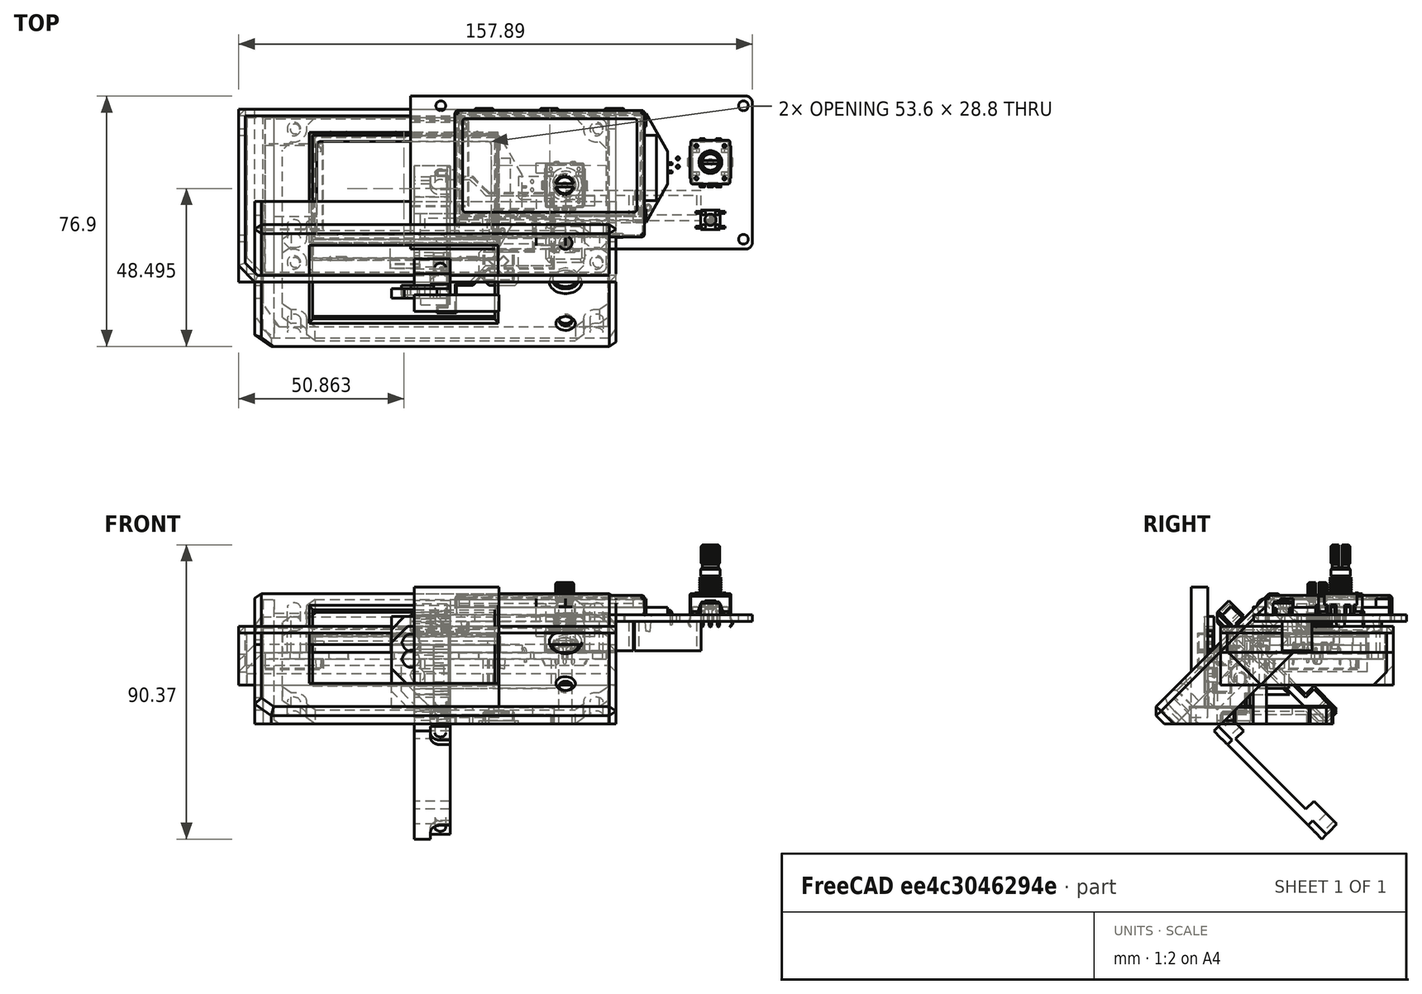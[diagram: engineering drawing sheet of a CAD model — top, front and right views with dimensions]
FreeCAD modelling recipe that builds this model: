
FCSTD DOCUMENT  (FreeCAD 0.18R16146 (Git))
Label: lcd-mount
License: All rights reserved
LicenseURL: http://en.wikipedia.org/wiki/All_rights_reserved
objects: Part::Box×50, Part::Chamfer×35, Part::Feature×26, Part::Cylinder×20, Part::Cut×20, Part::MultiFuse×19, App::Part×2, Part::Fillet×2
note: 172 computed .brp shape members not serialized (recipe doc carries the construction recipe); baked Part::Feature solids carry a one-line shape summary decoded from their .brp

FEATURE [Part::Feature] Part__Feature  label="backlight"
  Placement = pos=(66.893,35.0548,33.5073) rot=(0,0.707107,0.707107;3.14159rad)
  shape: bbox 66.3 x 33.5 x 10 mm, 77 faces (baked)
FEATURE [Part::Feature] Part__Feature001  label="lcd"
  Placement = pos=(30.968,36.0048,35.8073) rot=(1,0,0;1.5708rad)
  shape: bbox 56.5 x 40.6 x 5.3 mm, 42 faces (baked)
FEATURE [Part::Feature] Part__Feature002  label="PCB"
  Placement = pos=(40.393,33.6048,31.5073) rot=(0,0,1;0rad)
  shape: bbox 105 x 47 x 11 mm, 65 faces (baked)
FEATURE [Part::Feature] Part__Feature003  label="Tactal Switch - SMD (6mmx 6mmx 4"
  Placement = pos=(80.0049,19.0968,33.5073) rot=(0,0,1;0rad)
  shape: bbox 9.017 x 6.169 x 4.3 mm, 213 faces (baked)
FEATURE [Part::Feature] Part__Feature004  label="pec11r-4215k_l13-8_w12-4_h21-5"
  Placement = pos=(80.0049,36.8224,33.5073) rot=(1,0,0;1.5708rad)
  shape: bbox 13.86 x 14.85 x 25.2 mm, 388 faces (baked)
FEATURE [Part::Feature] Part__Feature005  label="LCD bezel"
  Placement = pos=(40.1054,33.7331,33.5073) rot=(0,0,1;0rad)
  shape: bbox 58.3 x 38.9 x 6 mm, 31 faces (baked)
FEATURE [App::Part] _2864Amini  label="12864Amini"
  Group = -> [Part__Feature,Part__Feature001,Part__Feature002,Part__Feature003,Part__Feature004,Part__Feature005]
  Origin = -> Origin
  Placement = pos=(128.127,156.765,-6.05529) rot=(0,0,1;0rad)
FEATURE [App::Part] Fysetc_12864_Display_Fysetc_Mini_12864_v1_v2  label="Fysetc_12864_Display_Fysetc Mini 12864 v1 v2"
  Group = -> [_2864Amini]
  Origin = -> Origin001
FEATURE [Part::Feature] Part__Feature005001  label="LCD bezel001"
  Placement = pos=(40.1054,33.7331,33.5073) rot=(0,0,1;0rad)
  shape: bbox 58.3 x 38.9 x 6 mm, 31 faces (baked)
FEATURE [Part::Feature] Part__Feature004001  label="pec11r-4215k_l13-8_w12-4_h21-006"
  Placement = pos=(80.0049,36.8224,33.5073) rot=(1,0,0;1.5708rad)
  shape: bbox 13.86 x 14.85 x 25.2 mm, 388 faces (baked)
FEATURE [Part::Feature] Part__Feature003001  label="Tactal Switch - SMD (6mmx 6mmx 005"
  Placement = pos=(80.0049,19.0968,33.5073) rot=(0,0,1;0rad)
  shape: bbox 9.017 x 6.169 x 4.3 mm, 213 faces (baked)
FEATURE [Part::Feature] Part__Feature002001  label="PCB001"
  Placement = pos=(40.393,33.6048,31.5073) rot=(0,0,1;0rad)
  shape: bbox 105 x 47 x 11 mm, 65 faces (baked)
FEATURE [Part::Feature] Part__Feature001001  label="lcd001"
  Placement = pos=(30.968,36.0048,35.8073) rot=(1,0,0;1.5708rad)
  shape: bbox 56.5 x 40.6 x 5.3 mm, 42 faces (baked)
FEATURE [Part::Feature] Part__Feature005002  label="backlight001"
  Placement = pos=(66.893,35.0548,33.5073) rot=(0,0.707107,0.707107;3.14159rad)
  shape: bbox 66.3 x 33.5 x 10 mm, 77 faces (baked)
FEATURE [Part::MultiFuse] Fusion
  Placement = pos=(-44.78,-7.11,-11.51) rot=(0,0,1;0rad)
  Shapes = -> [Part__Feature005002,Part__Feature001001,Part__Feature002001,Part__Feature003001,Part__Feature004001,Part__Feature005001]
FEATURE [Part::Box] Box  label="Cube"
  AttacherType = Attacher::AttachEngine3D
  Height = 2
  Length = 116
  Placement = pos=(-65,0,28) rot=(0,0,1;0rad)
  Width = 53
FEATURE [Part::Box] Box001  label="Cube001"
  AttacherType = Attacher::AttachEngine3D
  Height = 4
  Length = 56
  Placement = pos=(-42.25,13,28) rot=(0,0,1;0rad)
  Width = 32
FEATURE [Part::Cylinder] Cylinder
  Angle = 360
  AttacherType = Attacher::AttachEngine3D
  Height = 6
  Placement = pos=(45,6,20) rot=(0,0,1;0rad)
  Radius = 2.05
FEATURE [Part::Cylinder] Cylinder001
  Angle = 360
  AttacherType = Attacher::AttachEngine3D
  Height = 6
  Placement = pos=(45,47,20) rot=(0,0,1;0rad)
  Radius = 2.05
FEATURE [Part::Cylinder] Cylinder002
  Angle = 360
  AttacherType = Attacher::AttachEngine3D
  Height = 6
  Placement = pos=(-48,47,20) rot=(0,0,1;0rad)
  Radius = 2.05
FEATURE [Part::Cylinder] Cylinder003
  Angle = 360
  AttacherType = Attacher::AttachEngine3D
  Height = 6
  Placement = pos=(-48,6,20) rot=(0,0,1;0rad)
  Radius = 2.05
FEATURE [Part::Cylinder] Cylinder004
  Angle = 360
  AttacherType = Attacher::AttachEngine3D
  Height = 6
  Placement = pos=(-48,47,22) rot=(0,0,1;0rad)
  Radius = 4
FEATURE [Part::Cylinder] Cylinder005
  Angle = 360
  AttacherType = Attacher::AttachEngine3D
  Height = 6
  Placement = pos=(-48,6,22) rot=(0,0,1;0rad)
  Radius = 4
FEATURE [Part::Cylinder] Cylinder006
  Angle = 360
  AttacherType = Attacher::AttachEngine3D
  Height = 6
  Placement = pos=(45,47,22) rot=(0,0,1;0rad)
  Radius = 4
FEATURE [Part::Cylinder] Cylinder007
  Angle = 360
  AttacherType = Attacher::AttachEngine3D
  Height = 6
  Placement = pos=(45,6,22) rot=(0,0,1;0rad)
  Radius = 4
FEATURE [Part::MultiFuse] Fusion002
  Placement = pos=(0,0,2) rot=(0,0,1;0rad)
  Shapes = -> [Cylinder003,Cylinder002,Cylinder001,Cylinder]
FEATURE [Part::Box] Box002  label="Cube002"
  AttacherType = Attacher::AttachEngine3D
  Height = 16
  Length = 2.5
  Placement = pos=(48.5,0,12) rot=(0,0,1;0rad)
  Width = 53
FEATURE [Part::Box] Box003  label="Cube003"
  AttacherType = Attacher::AttachEngine3D
  Height = 16
  Length = 2.5
  Placement = pos=(-65,0,12) rot=(0,0,1;0rad)
  Width = 53
FEATURE [Part::Box] Box004  label="Cube004"
  AttacherType = Attacher::AttachEngine3D
  Height = 16
  Length = 116
  Placement = pos=(-65,0,12) rot=(0,0,1;0rad)
  Width = 2.5
FEATURE [Part::Box] Box005  label="Cube005"
  AttacherType = Attacher::AttachEngine3D
  Height = 16
  Length = 116
  Placement = pos=(-65,50.5,12) rot=(0,0,1;0rad)
  Width = 2.5
FEATURE [Part::Box] Box006  label="Cube006"
  AttacherType = Attacher::AttachEngine3D
  Height = 6
  Length = 111
  Placement = pos=(-60,50.5,0) rot=(0,0,1;0rad)
  Width = 2.5
FEATURE [Part::Box] Box007  label="Cube007"
  AttacherType = Attacher::AttachEngine3D
  Height = 6
  Length = 111
  Placement = pos=(-60,0,0) rot=(0,0,1;0rad)
  Width = 2.5
FEATURE [Part::Box] Box008  label="Cube008"
  AttacherType = Attacher::AttachEngine3D
  Height = 6
  Length = 2.5
  Placement = pos=(-60,0,0) rot=(0,0,1;0rad)
  Width = 53
FEATURE [Part::Box] Box009  label="Cube009"
  AttacherType = Attacher::AttachEngine3D
  Height = 6
  Length = 2.5
  Placement = pos=(48.5,0,0) rot=(0,0,1;0rad)
  Width = 53
FEATURE [Part::MultiFuse] Fusion003
  Placement = pos=(0,0,22) rot=(0,0,1;0rad)
  Shapes = -> [Box009,Box008,Box007,Box006]
FEATURE [Part::Box] Box010  label="Cube010"
  AttacherType = Attacher::AttachEngine3D
  Height = 6
  Length = 2.5
  Placement = pos=(-54,0,22) rot=(0,0,1;0rad)
  Width = 53
FEATURE [Part::Feature] Fusion003001  label="Fusion004"
  shape: bbox 111 x 53 x 6 mm, 10 faces (baked)
FEATURE [Part::Chamfer] Chamfer
  Base = -> Fusion003001
  Edges = 1 edges r=5: [Edge4]
FEATURE [Part::Chamfer] Chamfer001
  Base = -> Chamfer
  Edges = 1 edges r=5: [Edge26]
FEATURE [Part::Cylinder] Cylinder008
  Angle = 360
  AttacherType = Attacher::AttachEngine3D
  Height = 37
  Placement = pos=(35.5,30,0) rot=(0,0,1;0rad)
  Radius = 4
FEATURE [Part::Cylinder] Cylinder009  label="reset-btn-pos"
  Angle = 360
  AttacherType = Attacher::AttachEngine3D
  Height = 36
  Placement = pos=(35.5,12,0) rot=(0,0,1;0rad)
  Radius = 2
FEATURE [Part::Box] Box011  label="Cube011"
  AttacherType = Attacher::AttachEngine3D
  Height = 5.5
  Length = 10
  Placement = pos=(-68,14.5,16) rot=(0,0,1;0rad)
  Width = 30.5
FEATURE [Part::MultiFuse] Fusion003005
  Shapes = -> [Cylinder004,Cylinder007,Cylinder006,Cylinder005]
FEATURE [Part::Box] Box014  label="led-pos-1"
  AttacherType = Attacher::AttachEngine3D
  Height = 10
  Length = 3
  Placement = pos=(41.5,23.5,27) rot=(0,0,1;0rad)
  Width = 3
FEATURE [Part::Box] Box015  label="led-pos-2"
  AttacherType = Attacher::AttachEngine3D
  Height = 10
  Length = 3
  Placement = pos=(26.5,33.5,27) rot=(0,0,1;0rad)
  Width = 3
FEATURE [Part::Box] Box016  label="Cube013"
  AttacherType = Attacher::AttachEngine3D
  Height = 3
  Length = 11
  Width = 47
FEATURE [Part::Box] Box017  label="Cube014"
  AttacherType = Attacher::AttachEngine3D
  Height = 3.5
  Length = 11
  Placement = pos=(0,0,-3.5) rot=(0,0,1;0rad)
  Width = 6.5
FEATURE [Part::Box] Box018  label="Cube015"
  AttacherType = Attacher::AttachEngine3D
  Height = 3.5
  Length = 11
  Placement = pos=(0,37,-3.5) rot=(0,0,1;0rad)
  Width = 10
FEATURE [Part::Cylinder] Cylinder010
  Angle = 360
  AttacherType = Attacher::AttachEngine3D
  Height = 10
  Placement = pos=(3,3,0) rot=(0,0,1;0rad)
  Radius = 1.65
FEATURE [Part::Cylinder] Cylinder011
  Angle = 360
  AttacherType = Attacher::AttachEngine3D
  Height = 10
  Placement = pos=(3,44,0) rot=(0,0,1;0rad)
  Radius = 1.65
FEATURE [Part::MultiFuse] Fusion003007003
  Placement = pos=(0,0,-6) rot=(0,0,1;0rad)
  Shapes = -> [Cylinder011,Cylinder010]
FEATURE [Part::Box] Box020  label="a2"
  AttacherType = Attacher::AttachEngine3D
  Height = 54
  Length = 128
  Placement = pos=(-70,11.8171,-5.79763) rot=(1,0,0;0.785398rad)
  Width = 13
FEATURE [Part::Feature] Box021001  label="a1"
  Placement = pos=(0,26,-1) rot=(0,0,1;0rad)
  shape: bbox 130 x 38.18 x 38.18 mm, 6 faces (baked)
FEATURE [Part::MultiFuse] Fusion003007004
  Shapes = -> [Box016,Box018,Box017]
FEATURE [Part::Cut] Cut004005004004  label="lcd-arm"
  Base = -> Fusion003007004
  Placement = pos=(0,0,0) rot=(1,0,0;3.14159rad)
  Tool = -> Fusion003007003
FEATURE [Part::Feature] Cut004005004003001  label="lcd-base001"
  Placement = pos=(0,0,-17.26) rot=(0,0,1;0rad)
  shape: bbox 111 x 44.52 x 40.02 mm, 69 faces (baked)
FEATURE [Part::Box] Box021002  label="Cube020"
  AttacherType = Attacher::AttachEngine3D
  Height = 2
  Length = 6
  Placement = pos=(0,-6,-3) rot=(0,0,1;0rad)
  Width = 6
FEATURE [Part::Box] Box021003  label="Cube021"
  AttacherType = Attacher::AttachEngine3D
  Height = 2
  Length = 6
  Placement = pos=(0,-47,-3) rot=(0,0,1;0rad)
  Width = 6
FEATURE [Part::Fillet] Fillet
  Base = -> Box021003
  Edges = 1 edges r=3: [Edge7]
FEATURE [Part::Fillet] Fillet001
  Base = -> Box021002
  Edges = 1 edges r=3: [Edge5]
FEATURE [Part::MultiFuse] Fusion003007005
  Shapes = -> [Fillet001,Fillet]
FEATURE [Part::Cut] Cut004005004003002
  Base = -> Cut004005004004
  Placement = pos=(0,0,0) rot=(0,0.382683,0.92388;3.14159rad)
  Tool = -> Fusion003007005
FEATURE [Part::Feature] Cut004005004003002001  label="Cut004005004003003"
  Placement = pos=(0,0,35.36) rot=(0,0,1;0rad)
  shape: bbox 11 x 37.83 x 37.83 mm, 20 faces (baked)
FEATURE [Part::Box] Box021005  label="Cube023"
  AttacherType = Attacher::AttachEngine3D
  Height = 10
  Length = 10
  Placement = pos=(30.5,7,23) rot=(0,0,1;0rad)
  Width = 10
FEATURE [Part::Chamfer] Chamfer012
  Base = -> Box021005
  Edges = 4 edges r=0.5: [Edge1,Edge3,Edge5,Edge7]
FEATURE [Part::Chamfer] Chamfer016  label="mounter-angle"
  Base = -> Cut004005004003002001
  Edges = 2 edges r=1.5: [Edge25,Edge27]
FEATURE [Part::Box] Box021010  label="Cube028"
  AttacherType = Attacher::AttachEngine3D
  Height = 5
  Length = 11
  Placement = pos=(-11,8,5) rot=(0,0,1;0rad)
  Width = 19
FEATURE [Part::Feature] Chamfer016001  label="mounter-angle001"
  shape: bbox 11 x 36.77 x 36.77 mm, 22 faces (baked)
FEATURE [Part::Chamfer] Chamfer016002
  Base = -> Box021010
  Edges = 1 edges r=3: [Edge12]
FEATURE [Part::Box] Box021012  label="Cube030"
  AttacherType = Attacher::AttachEngine3D
  Height = 4
  Length = 11
  Placement = pos=(-11,3,25) rot=(0,0,1;0rad)
  Width = 5
FEATURE [Part::Chamfer] Chamfer016003
  Base = -> Box021012
  Edges = 1 edges r=3: [Edge12]
FEATURE [Part::Cylinder] Cylinder013
  Angle = 360
  AttacherType = Attacher::AttachEngine3D
  Height = 10
  Placement = pos=(-3,6,15) rot=(0,-1,0;1.5708rad)
  Radius = 2
FEATURE [Part::Box] Box021011  label="Cube029"
  AttacherType = Attacher::AttachEngine3D
  Height = 22
  Length = 6
  Placement = pos=(-11,3,5) rot=(0,0,1;0rad)
  Width = 6
FEATURE [Part::Chamfer] Chamfer016004
  Base = -> Box021011
  Edges = 1 edges r=1: [Edge12]
FEATURE [Part::Cut] Cut004005004003002006
  Base = -> Chamfer016004
  Tool = -> Cylinder013
FEATURE [Part::Chamfer] Chamfer016005
  Base = -> Cut004005004003002006
  Edges = 1 edges r=1: [Edge12]
FEATURE [Part::Chamfer] Chamfer016006
  Base = -> Chamfer016002
  Edges = 1 edges r=1: [Edge12]
FEATURE [Part::MultiFuse] Fusion003007008002
  Placement = pos=(0,0,-1) rot=(0,0,1;0rad)
  Shapes = -> [Chamfer016006,Chamfer016005,Chamfer016003,Chamfer016001]
FEATURE [Part::Box] Box021013  label="Cube031"
  AttacherType = Attacher::AttachEngine3D
  Height = 19.8
  Length = 5
  Placement = pos=(-5,3,5) rot=(0,0,1;0rad)
  Width = 6
FEATURE [Part::Box] Box021014  label="Cube032"
  AttacherType = Attacher::AttachEngine3D
  Height = 5.2
  Length = 5
  Placement = pos=(-5,7.8,5) rot=(0,0,1;0rad)
  Width = 2
FEATURE [Part::Cylinder] Cylinder014
  Angle = 360
  AttacherType = Attacher::AttachEngine3D
  Height = 2
  Placement = pos=(-3e-15,6,15) rot=(0,-1,0;1.5708rad)
  Radius = 3
FEATURE [Part::Cylinder] Cylinder015
  Angle = 360
  AttacherType = Attacher::AttachEngine3D
  Height = 10
  Placement = pos=(-3e-15,6,15) rot=(0,-1,0;1.5708rad)
  Radius = 1.65
FEATURE [Part::Box] Box021015  label="Cube033"
  AttacherType = Attacher::AttachEngine3D
  Height = 40
  Length = 26
  Placement = pos=(-11,-9,2) rot=(0,0,1;0rad)
  Width = 5
FEATURE [Part::Box] Box021016  label="Cube034"
  AttacherType = Attacher::AttachEngine3D
  Height = 4
  Length = 5
  Placement = pos=(-5,-5,13) rot=(0,0,1;0rad)
  Width = 1
FEATURE [Part::Box] Box021018  label="Cube036"
  AttacherType = Attacher::AttachEngine3D
  Height = 5
  Length = 5
  Placement = pos=(-5,-4,5) rot=(0,0,1;0rad)
  Width = 7
FEATURE [Part::Box] Box021019  label="Cube037"
  AttacherType = Attacher::AttachEngine3D
  Height = 5
  Length = 5
  Placement = pos=(-5,-4,18) rot=(0,0,1;0rad)
  Width = 7
FEATURE [Part::Box] Box021020  label="Cube038"
  AttacherType = Attacher::AttachEngine3D
  Height = 18
  Length = 15
  Placement = pos=(-15,-4,5) rot=(0,0,1;0rad)
  Width = 3
FEATURE [Part::Cylinder] Cylinder016
  Angle = 360
  AttacherType = Attacher::AttachEngine3D
  Height = 10
  Placement = pos=(-10,3e-15,12) rot=(1,0,0;1.5708rad)
  Radius = 2.15
FEATURE [Part::Chamfer] Chamfer016007
  Base = -> Box021013
  Edges = 1 edges r=3: [Edge12]
FEATURE [Part::Chamfer] Chamfer016008
  Base = -> Chamfer016007
  Edges = 1 edges r=1: [Edge11]
FEATURE [Part::Cut] Cut004005004003002007
  Base = -> Chamfer016008
  Tool = -> Box021014
FEATURE [Part::Cut] Cut004005004003002008  label="back-mount"
  Base = -> Cut004005004003002007
  Placement = pos=(0,0,-1) rot=(0,0,1;0rad)
  Tool = -> Cylinder015
FEATURE [Part::Feature] Cut004005004003002008001  label="block-mount-std"
  shape: bbox 5 x 6 x 19.8 mm, 11 faces (baked)
FEATURE [Part::Cylinder] Cylinder017
  Angle = 360
  AttacherType = Attacher::AttachEngine3D
  Height = 10
  Placement = pos=(-11.8,3e-15,12) rot=(1,0,0;1.5708rad)
  Radius = 0.5
FEATURE [Part::MultiFuse] Fusion003007008003
  Placement = pos=(0,0,3) rot=(0,0,1;0rad)
  Shapes = -> [Cylinder017,Cylinder016]
FEATURE [Part::Chamfer] Chamfer016011  label="mount-arm-r1"
  Base = -> Fusion003007008002
  Edges = 2 edges r=1: [Edge99,Edge115]
FEATURE [Part::Cut] Cut004005004003002008002
  Base = -> Box021020
  Tool = -> Fusion003007008003
FEATURE [Part::Chamfer] Chamfer016012
  Base = -> Cut004005004003002008002
  Edges = 1 edges r=3: [Edge2]
FEATURE [Part::Chamfer] Chamfer016013
  Base = -> Chamfer016012
  Edges = 1 edges r=5: [Edge3]
FEATURE [Part::Feature] Fusion003007008004001  label="4040-mount001"
  shape: bbox 15 x 14 x 19.8 mm, 27 faces (baked)
FEATURE [Part::Chamfer] Chamfer016014  label="4040-mount-exp"
  Base = -> Fusion003007008004001
  Edges = 19 edges r=0.4: [Edge3,Edge9,Edge11,Edge12,Edge13,Edge32,Edge43,Edge46,Edge47,Edge51,Edge52,Edge58,Edge61,Edge62,Edge66,Edge70,Edge73,Edge74,Edge76]
FEATURE [Part::Box] Box021021  label="Cube039"
  AttacherType = Attacher::AttachEngine3D
  Height = 4
  Length = 9.5
  Placement = pos=(10.25,0.25,0) rot=(0,0,1;0rad)
  Width = 9.5
FEATURE [Part::Box] Box021022  label="Cube040"
  AttacherType = Attacher::AttachEngine3D
  Height = 1
  Length = 12
  Placement = pos=(9,-1,0) rot=(0,0,1;0rad)
  Width = 11
FEATURE [Part::Feature] Fusion003007008004003002001  label="Fusion003007008004003003"
  Placement = pos=(15,5,3) rot=(0,0,1;0rad)
  shape: bbox 5.657 x 5.657 x 10 mm, 14 faces (baked)
FEATURE [Part::Cut] Cut004005004003002008006
  Base = -> Box021021
  Tool = -> Fusion003007008004003002001
FEATURE [Part::Cylinder] Cylinder018
  Angle = 360
  AttacherType = Attacher::AttachEngine3D
  Height = 0.5
  Placement = pos=(15,5,0) rot=(0,0,1;0rad)
  Radius = 3
FEATURE [Part::Chamfer] Chamfer016020
  Base = -> Cut004005004003002008006
  Edges = 8 edges r=0.5: [Edge1,Edge2,Edge3,Edge6,Edge7,Edge8,Edge9,Edge23]
FEATURE [Part::Chamfer] Chamfer016021
  Base = -> Chamfer016020
  Edges = 12 edges r=0.2: [Edge33,Edge34,Edge35,Edge36,Edge37,Edge38,Edge39,Edge40,Edge41,Edge42,Edge43,Edge44]
FEATURE [Part::MultiFuse] Fusion003007008004003002003  label="4040-base"
  Shapes = -> [Box021016,Box021019,Box021018,Cut004005004003002008,Chamfer016013]
FEATURE [Part::Box] Box021023  label="Cube041"
  AttacherType = Attacher::AttachEngine3D
  Height = 28
  Length = 18
  Placement = pos=(-18,-5,5) rot=(0,0,1;0rad)
  Width = 3
FEATURE [Part::Box] Box021024  label="Cube042"
  AttacherType = Attacher::AttachEngine3D
  Height = 6
  Length = 9
  Placement = pos=(-9,-7,22) rot=(0,0,1;0rad)
  Width = 2
FEATURE [Part::Cylinder] Cylinder019
  Angle = 360
  AttacherType = Attacher::AttachEngine3D
  Height = 10
  Placement = pos=(-12,-10,20) rot=(-1,0,0;1.5708rad)
  Radius = 2.6
FEATURE [Part::Box] Box021025  label="Cube043"
  AttacherType = Attacher::AttachEngine3D
  Height = 5
  Length = 5
  Placement = pos=(-5,-5,5) rot=(0,0,1;0rad)
  Width = 8
FEATURE [Part::Box] Box021026  label="Cube044"
  AttacherType = Attacher::AttachEngine3D
  Height = 5
  Length = 5
  Placement = pos=(-5,-5,18.8) rot=(0,0,1;0rad)
  Width = 8
FEATURE [Part::Cylinder] Cylinder020
  Angle = 360
  AttacherType = Attacher::AttachEngine3D
  Height = 10
  Placement = pos=(-14.3,-10,20) rot=(-1,0,0;1.5708rad)
  Radius = 0.5
FEATURE [Part::MultiFuse] Fusion003007008004003002004
  Placement = pos=(0,0,5) rot=(0,0,1;0rad)
  Shapes = -> [Cylinder020,Cylinder019]
FEATURE [Part::Feature] Cut004005004003002008001001  label="block-mount-std001"
  shape: bbox 5 x 6 x 19.8 mm, 11 faces (baked)
FEATURE [Part::Feature] Fusion003007008004003002005001  label="3030-mount-5mm-lower-base001"
  shape: bbox 18 x 16 x 26 mm, 27 faces (baked)
FEATURE [Part::Chamfer] Chamfer016025
  Base = -> Fusion003007008004003002005001
  Edges = 13 edges r=0.4: [Edge6,Edge9,Edge11,Edge13,Edge14,Edge55,Edge56,Edge57,Edge58,Edge59,Edge60,Edge61,Edge62]
FEATURE [Part::Chamfer] Chamfer016026  label="3030-5mm-lower"
  Base = -> Chamfer016025
  Edges = 5 edges r=0.4: [Edge42,Edge43,Edge44,Edge45,Edge46]
FEATURE [Part::Cut] Cut004005004003002008001002
  Base = -> Box021023
  Tool = -> Fusion003007008004003002004
FEATURE [Part::MultiFuse] Fusion003007008004003002005002
  Shapes = -> [Cut004005004003002008001002,Box021024,Cut004005004003002008001001,Box021026,Box021025]
FEATURE [Part::Feature] Fusion003007008004003002005002001  label="Fusion003007008004003002005003"
  shape: bbox 18 x 16 x 29 mm, 24 faces (baked)
FEATURE [Part::Chamfer] Chamfer016027
  Base = -> Fusion003007008004003002005002001
  Edges = 1 edges r=4: [Edge22]
FEATURE [Part::Chamfer] Chamfer016028
  Base = -> Chamfer016027
  Edges = 1 edges r=4: [Edge36]
FEATURE [Part::Chamfer] Chamfer016029
  Base = -> Chamfer016028
  Edges = 1 edges r=12: [Edge21]
FEATURE [Part::MultiFuse] Fusion003007008004003002005002002
  Shapes = -> [Box002,Box003,Box004,Box005]
FEATURE [Part::Feature] Fusion003007008004003002005002002001  label="Fusion003007008004003002005002003"
  shape: bbox 116 x 53 x 16 mm, 10 faces (baked)
FEATURE [Part::Chamfer] Chamfer016031
  Base = -> Fusion003007008004003002005002002001
  Edges = 1 edges r=5: [Edge4]
FEATURE [Part::Chamfer] Chamfer016032
  Base = -> Chamfer016031
  Edges = 1 edges r=5: [Edge26]
FEATURE [Part::Cut] Cut004005004003002008001003
  Base = -> Chamfer016032
  Tool = -> Box011
FEATURE [Part::MultiFuse] Fusion003002
  Shapes = -> [Chamfer001,Box010]
FEATURE [Part::Chamfer] Chamfer003
  Base = -> Fusion003002
  Edges = 4 edges r=10: [Edge40,Edge42,Edge44,Edge46]
FEATURE [Part::MultiFuse] Fusion003006
  Shapes = -> [Chamfer003,Fusion003005]
FEATURE [Part::Cut] Cut004002
  Base = -> Fusion003006
  Tool = -> Fusion002
FEATURE [Part::Box] Box021027  label="Cube045"
  AttacherType = Attacher::AttachEngine3D
  Height = 12
  Length = 10
  Placement = pos=(-64,-2,18) rot=(0,0,1;0rad)
  Width = 57
FEATURE [Part::Cut] Cut004005004003002008001004
  Base = -> Cut004002
  Tool = -> Box021027
FEATURE [Part::Chamfer] Chamfer016033
  Base = -> Box
  Edges = 1 edges r=5: [Edge1]
FEATURE [Part::Cut] Cut
  Base = -> Chamfer016033
  Tool = -> Box001
FEATURE [Part::Cut] Cut004005004003002008001005
  Base = -> Cut
  Tool = -> Cylinder008
FEATURE [Part::Cut] Cut004005004003002008001006
  Base = -> Cut004005004003002008001005
  Tool = -> Chamfer012
FEATURE [Part::MultiFuse] Fusion003007008004003002005002002002  label="LCD-base"
  Shapes = -> [Cut004005004003002008001006,Cut004005004003002008001004,Cut004005004003002008001003]
FEATURE [Part::Feature] Fusion003007008004003002005002002002001  label="LCD-base001"
  shape: bbox 116 x 53 x 18 mm, 56 faces (baked)
FEATURE [Part::Chamfer] Chamfer016034
  Base = -> Fusion003007008004003002005002002002001
  Edges = 8 edges r=2: [Edge1,Edge2,Edge3,Edge4,Edge5,Edge90,Edge123,Edge124]
FEATURE [Part::Chamfer] Chamfer016035
  Base = -> Chamfer016034
  Edges = 13 edges r=1: [Edge6,Edge7,Edge8,Edge9,Edge10,Edge11,Edge12,Edge13,Edge14,Edge15,Edge16,Edge17,Edge18]
FEATURE [Part::Cut] Cut004005004003002008001007
  Base = -> Chamfer016035
  Tool = -> Box020
FEATURE [Part::Cut] Cut004005004003002008001008  label="LCD-r2"
  Base = -> Cut004005004003002008001007
  Tool = -> Box021001
FEATURE [Part::Box] Box021028  label="Cube046"
  AttacherType = Attacher::AttachEngine3D
  Height = 3
  Length = 12
  Placement = pos=(-1,0,0) rot=(0,0,1;0rad)
  Width = 31.5
FEATURE [Part::Box] Box021029  label="Cube047"
  AttacherType = Attacher::AttachEngine3D
  Height = 5.5
  Length = 13
  Placement = pos=(-1,-1,0) rot=(0,0,1;0rad)
  Width = 33.5
FEATURE [Part::Box] Box021030  label="Cube048"
  AttacherType = Attacher::AttachEngine3D
  Height = 2.5
  Length = 20
  Placement = pos=(12,4,3) rot=(0,0,1;0rad)
  Width = 23.5
FEATURE [Part::Box] Box021031  label="Cube049"
  AttacherType = Attacher::AttachEngine3D
  Height = 4
  Length = 12
  Placement = pos=(13.5,9.5,3) rot=(0,0,1;0rad)
  Width = 12.5
FEATURE [Part::Box] Box021032  label="Cube050"
  AttacherType = Attacher::AttachEngine3D
  Height = 4
  Length = 20
  Placement = pos=(12,4,0) rot=(0,0,1;0rad)
  Width = 1
FEATURE [Part::Box] Box021033  label="Cube051"
  AttacherType = Attacher::AttachEngine3D
  Height = 4
  Length = 20
  Placement = pos=(12,26.5,0) rot=(0,0,1;0rad)
  Width = 1
FEATURE [Part::Box] Box021034  label="Cube052"
  AttacherType = Attacher::AttachEngine3D
  Height = 4
  Length = 1
  Placement = pos=(31,4,0) rot=(0,0,1;0rad)
  Width = 23.5
FEATURE [Part::Box] Box021035  label="Cube053"
  AttacherType = Attacher::AttachEngine3D
  Height = 3
  Length = 1
  Placement = pos=(11,5,0) rot=(0,0,1;0rad)
  Width = 21.5
FEATURE [Part::Cut] Cut004005004003002008001012
  Base = -> Box021030
  Tool = -> Box021031
FEATURE [Part::MultiFuse] Fusion003007008004003002005002002002002
  Shapes = -> [Box021032,Box021034,Box021033]
FEATURE [Part::Cut] Cut004005004003002008001013
  Base = -> Box021029
  Tool = -> Box021028
FEATURE [Part::Chamfer] Chamfer016036
  Base = -> Cut004005004003002008001013
  Edges = 2 edges r=5: [Edge19,Edge23]
FEATURE [Part::Chamfer] Chamfer016037
  Base = -> Chamfer016036
  Edges = 2 edges r=5: [Edge23,Edge28]
FEATURE [Part::Cut] Cut004005004003002008001014
  Base = -> Chamfer016037
  Tool = -> Box021035
FEATURE [Part::Box] Box021036  label="Cube054"
  AttacherType = Attacher::AttachEngine3D
  Height = 5.5
  Length = 6
  Placement = pos=(-4,32.5,0) rot=(0,0,1;0rad)
  Width = 2
FEATURE [Part::Box] Box021037  label="Cube055"
  AttacherType = Attacher::AttachEngine3D
  Height = 5.5
  Length = 6
  Placement = pos=(-4,-9.5,0) rot=(0,0,1;0rad)
  Width = 2
FEATURE [Part::Box] Box021038  label="Cube056"
  AttacherType = Attacher::AttachEngine3D
  Height = 5.5
  Length = 3
  Placement = pos=(-1,-9.5,0) rot=(0,0,1;0rad)
  Width = 9
FEATURE [Part::MultiFuse] Fusion003007008004003002005002002002003  label="led-cover-base"
  Shapes = -> [Box021036,Box021038,Box021037,Cut004005004003002008001014,Fusion003007008004003002005002002002002,Cut004005004003002008001012]
FEATURE [Part::Feature] Fusion003007008004003002005002002002003001  label="led-cover-base001"
  shape: bbox 36 x 44 x 5.5 mm, 30 faces (baked)
FEATURE [Part::Chamfer] Chamfer016038  label="led-cover-r2"
  Base = -> Fusion003007008004003002005002002002003001
  Edges = 26 edges r=0.4: [Edge2,Edge3,Edge7,Edge9,Edge10,Edge12,Edge16,Edge19,Edge20,Edge21,Edge22,Edge23,Edge24,Edge25,Edge26,Edge27,Edge28,Edge29,Edge30,Edge31,Edge32,Edge33,Edge37,Edge80,Edge83,Edge84]
FEATURE [Part::Chamfer] Chamfer016039
  Base = -> Box021022
  Edges = 1 edges r=3: [Edge1]
FEATURE [Part::Chamfer] Chamfer016040
  Base = -> Chamfer016039
  Edges = 3 edges r=1: [Edge3,Edge12,Edge15]
FEATURE [Part::MultiFuse] Fusion003007008004003002005002002002003002  label="button-r2"
  Shapes = -> [Chamfer016040,Chamfer016021,Cylinder018]
FEATURE [Part::Box] Box021039  label="Cube057"
  AttacherType = Attacher::AttachEngine3D
  Height = 10
  Length = 10
  Placement = pos=(-5,3,17.8) rot=(0,0,1;0rad)
  Width = 10
FEATURE [Part::Chamfer] Chamfer016041
  Base = -> Box021039
  Edges = 1 edges r=6: [Edge9]
FEATURE [Part::Cut] Cut004005004003002008001015
  Base = -> Chamfer016029
  Tool = -> Chamfer016041
FEATURE [Part::Chamfer] Chamfer016042  label="3030-arm-100-lower-r1f1"
  Base = -> Cut004005004003002008001015
  Edges = 20 edges r=0.4: [Edge6,Edge9,Edge25,Edge28,Edge29,Edge30,Edge31,Edge32,Edge33,Edge34,Edge35,Edge36,Edge37,Edge38,Edge39,Edge40,Edge41,Edge42,Edge43,Edge44]
